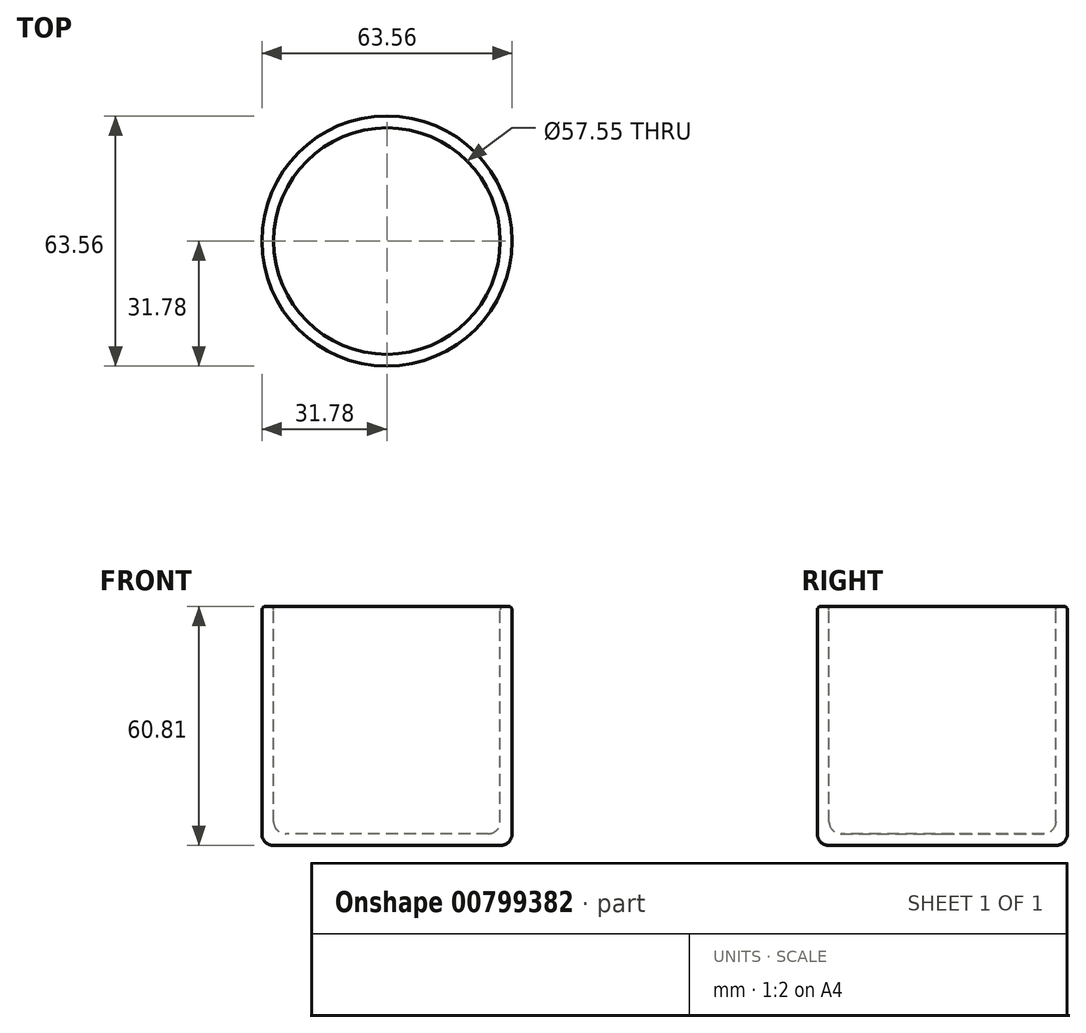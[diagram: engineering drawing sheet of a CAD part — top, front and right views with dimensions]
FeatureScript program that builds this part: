
annotation { "Feature Type Name" : "Feature", "Feature Type Description" : "" }
export const myFeature = defineFeature(function(context is Context, id is Id, definition is map)
    precondition{}
    {
        {
            var Q0;
            Q0=qCreatedBy(makeId("Front.planeOp"),FACE);
            var sketch = newSketch(context, id + "F0", { "sketchPlane" : qUnion([Q0])});
            skLineSegment(sketch, "E0", {"start": v(-5.9, -31.09) * mm, "end": v(25.78, -31.09) * mm});
            skLineSegment(sketch, "E1", {"start": v(28.78, -28.09) * mm, "end": v(28.78, 28.26) * mm});
            skLineSegment(sketch, "E2.0", {"start": v(31.78, -31.09) * mm, "end": v(31.78, 28.26) * mm});
            skLineSegment(sketch, "E2.1", {"start": v(-5.9, -34.09) * mm, "end": v(28.78, -34.09) * mm});
            skPoint(sketch, "E3.visualSharp", {"position": v(28.78, -31.09) * mm});
            skArc(sketch, "E3.filletArc", {"start": v(25.78, -31.09) * mm, "mid": v(27.9, -30.21) * mm, "end": v(28.78, -28.09) * mm});
            skPoint(sketch, "E4.visualSharp", {"position": v(31.78, -34.09) * mm});
            skArc(sketch, "E4.filletArc", {"start": v(28.78, -34.09) * mm, "mid": v(30.9, -33.21) * mm, "end": v(31.78, -31.09) * mm});
            skLineSegment(sketch, "E5", {"start": v(23.64, 26.72) * mm, "end": v(36.74, 26.72) * mm});
            skLineSegment(sketch, "E6", {"start": v(0, 52.67) * mm, "end": v(0, -68.6) * mm});
            skSolve(sketch);
        }
        {
            var Q0;
            {var subQ7=sQuery(id+"F0.wireOp",EDGE,"E3.filletArc");Q0=makeQuery(id+"F0.imprint","IMPRINT",FACE,{"disambiguationData":[TD([[makeQuery(id+"F0.imprint","IMPRINT",EDGE,{"derivedFrom":subQ7}),-1.0]])]});}
            var Q1;
            Q1=sQuery(id+"F0.wireOp",EDGE,"E6");
            revolve(context, id + "F1", {"surfaceOperationType" : NewSurfaceOperationType.NEW, "entities" : qUnion([Q0]), "axis" : qUnion([Q1]), "revolveType" : RevolveType.FULL});
        }
        {
            var Q0;
            Q0=makeQuery(id+"F1.opRevolve","SWEPT_EDGE",EDGE,{"disambiguationData":[OSD([sQuery(id+"F0.wireOp",EDGE,"E1"),sQuery(id+"F0.wireOp",EDGE,"E5")])]});
            fillet(context, id + "F2", {"entities" : qUnion([Q0]), "radius" : 1 * mm, "tangentPropagation" : true, "allowEdgeOverflow" : false});
        }
        {
            var Q0;
            Q0=makeQuery(id+"F1.opRevolve","SWEPT_EDGE",EDGE,{"disambiguationData":[OSD([sQuery(id+"F0.wireOp",EDGE,"E2.0"),sQuery(id+"F0.wireOp",EDGE,"E5")])]});
            fillet(context, id + "F3", {"entities" : qUnion([Q0]), "radius" : 1 * mm, "tangentPropagation" : true, "allowEdgeOverflow" : false});
        }
    });
